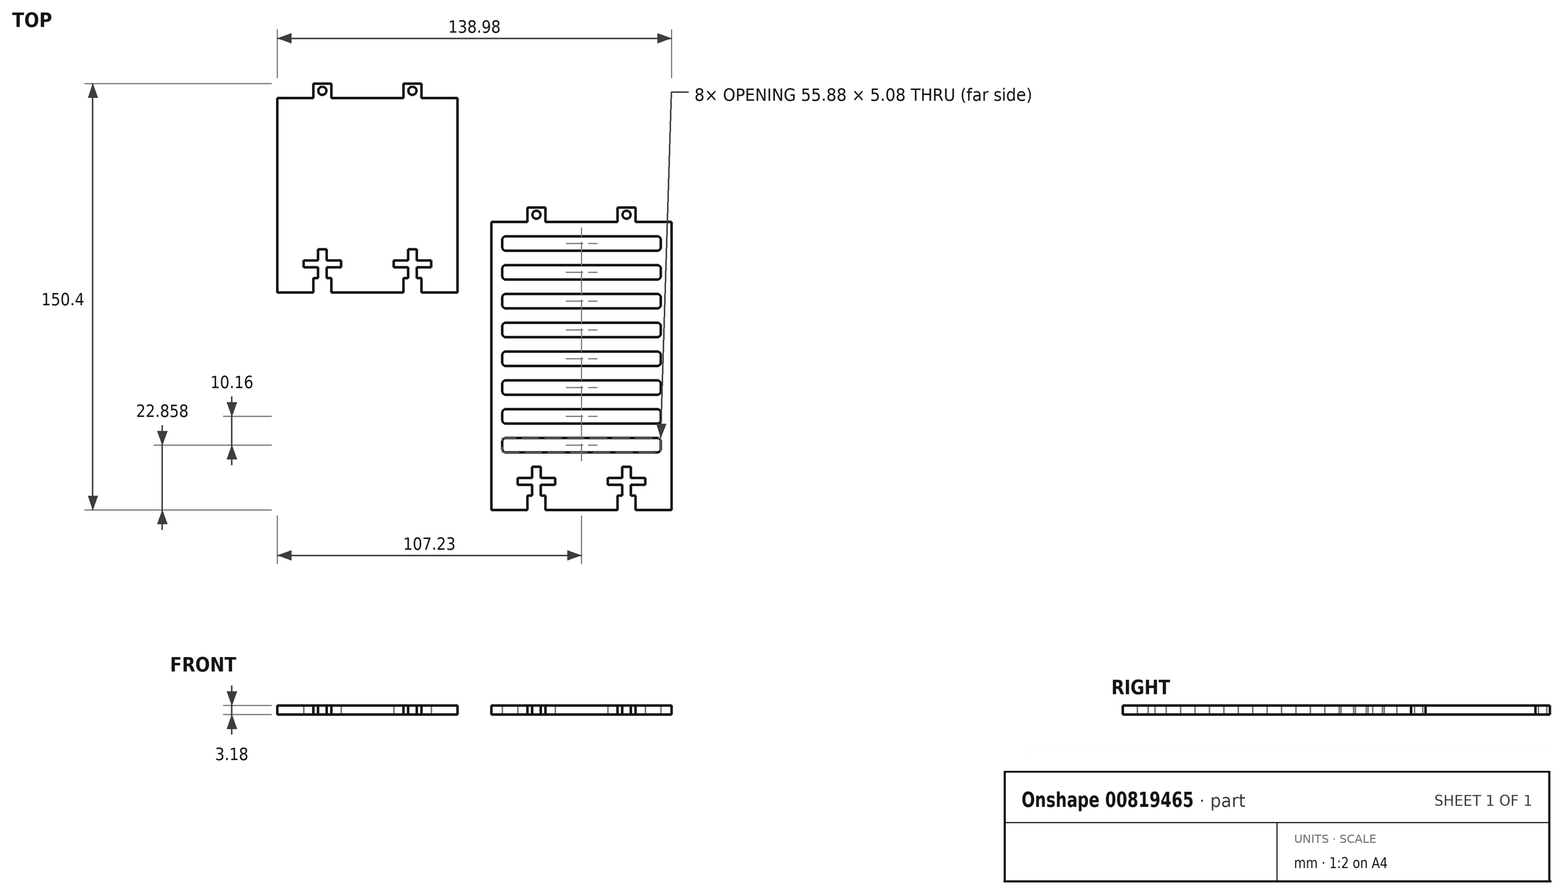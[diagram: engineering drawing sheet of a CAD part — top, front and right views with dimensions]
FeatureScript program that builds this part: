
annotation { "Feature Type Name" : "Feature", "Feature Type Description" : "" }
export const myFeature = defineFeature(function(context is Context, id is Id, definition is map)
    precondition{}
    {
        {
            var Q0;
            Q0=qCreatedBy(makeId("Top.planeOp"),FACE);
            var sketch = newSketch(context, id + "F0", { "sketchPlane" : qUnion([Q0])});
            skLineSegment(sketch, "E0.bottom", {"start": v(-19.79, 5.08) * mm, "end": v(-21.44, 5.08) * mm});
            skLineSegment(sketch, "E0.top", {"start": v(-7.09, 68.58) * mm, "end": v(-19.79, 68.58) * mm});
            skLineSegment(sketch, "E0.left", {"start": v(-7.09, 5.08) * mm, "end": v(-7.09, 68.58) * mm});
            skLineSegment(sketch, "E0.right", {"start": v(-70.59, 5.08) * mm, "end": v(-70.59, 68.58) * mm});
            skPoint(sketch, "E0.middle", {"position": v(-38.84, 36.83) * mm});
            skLineSegment(sketch, "E1", {"start": v(-54.71, 15.24) * mm, "end": v(-53.19, 15.24) * mm});
            skLineSegment(sketch, "E2", {"start": v(-53.19, 15.24) * mm, "end": v(-53.19, 11.28) * mm});
            skLineSegment(sketch, "E3", {"start": v(-53.19, 11.28) * mm, "end": v(-48.1, 11.28) * mm});
            skLineSegment(sketch, "E4", {"start": v(-48.1, 11.28) * mm, "end": v(-48.1, 8.89) * mm});
            skLineSegment(sketch, "E5", {"start": v(-48.1, 8.9) * mm, "end": v(-53.19, 8.9) * mm});
            skLineSegment(sketch, "E6", {"start": v(-53.19, 8.89) * mm, "end": v(-53.19, 5.08) * mm});
            skLineSegment(sketch, "E7.MirrorCS", {"start": v(-56.24, 15.24) * mm, "end": v(-56.24, 11.28) * mm});
            skLineSegment(sketch, "E8.MirrorCS", {"start": v(-54.71, 15.24) * mm, "end": v(-56.24, 15.24) * mm});
            skLineSegment(sketch, "E9.MirrorCS", {"start": v(-56.24, 11.28) * mm, "end": v(-61.32, 11.28) * mm});
            skLineSegment(sketch, "E10.MirrorCS", {"start": v(-61.32, 11.28) * mm, "end": v(-61.32, 8.9) * mm});
            skLineSegment(sketch, "E11.MirrorCS", {"start": v(-61.32, 8.9) * mm, "end": v(-56.24, 8.9) * mm});
            skLineSegment(sketch, "E12.MirrorCS", {"start": v(-56.24, 8.89) * mm, "end": v(-56.24, 5.08) * mm});
            skLineSegment(sketch, "E13.trimOffspring", {"start": v(-56.24, 5.08) * mm, "end": v(-57.89, 5.08) * mm});
            skLineSegment(sketch, "E14", {"start": v(-38.84, 36.83) * mm, "end": v(-38.84, 5.08) * mm, "construction": true});
            skLineSegment(sketch, "E15.MirrorCS", {"start": v(-24.49, 8.89) * mm, "end": v(-24.49, 5.08) * mm});
            skLineSegment(sketch, "E16.MirrorCS", {"start": v(-29.57, 8.9) * mm, "end": v(-24.49, 8.9) * mm});
            skLineSegment(sketch, "E17.MirrorCS", {"start": v(-29.57, 11.28) * mm, "end": v(-29.57, 8.89) * mm});
            skLineSegment(sketch, "E18.MirrorCS", {"start": v(-24.49, 11.28) * mm, "end": v(-29.57, 11.28) * mm});
            skLineSegment(sketch, "E19.MirrorCS", {"start": v(-24.49, 15.24) * mm, "end": v(-24.49, 11.28) * mm});
            skLineSegment(sketch, "E20.MirrorCS", {"start": v(-22.96, 15.24) * mm, "end": v(-24.49, 15.24) * mm});
            skLineSegment(sketch, "E21.MirrorCS", {"start": v(-22.96, 15.24) * mm, "end": v(-21.44, 15.24) * mm});
            skLineSegment(sketch, "E22.MirrorCS", {"start": v(-21.44, 15.24) * mm, "end": v(-21.44, 11.28) * mm});
            skLineSegment(sketch, "E23.MirrorCS", {"start": v(-21.44, 11.28) * mm, "end": v(-16.36, 11.28) * mm});
            skLineSegment(sketch, "E24.MirrorCS", {"start": v(-16.36, 11.28) * mm, "end": v(-16.36, 8.9) * mm});
            skLineSegment(sketch, "E25.MirrorCS", {"start": v(-16.36, 8.9) * mm, "end": v(-21.44, 8.9) * mm});
            skLineSegment(sketch, "E26.MirrorCS", {"start": v(-21.44, 8.9) * mm, "end": v(-21.44, 5.08) * mm});
            skLineSegment(sketch, "E27.trimOffspring", {"start": v(-24.49, 5.08) * mm, "end": v(-26.14, 5.08) * mm});
            skPoint(sketch, "E28", {"position": v(-54.71, 68.58) * mm});
            skPoint(sketch, "E29", {"position": v(-51.54, 68.58) * mm});
            skLineSegment(sketch, "E30", {"start": v(-54.71, 68.58) * mm, "end": v(-54.71, 51.26) * mm, "construction": true});
            skPoint(sketch, "E31.MirrorP", {"position": v(-57.89, 68.58) * mm});
            skLineSegment(sketch, "E32.trimOffspring", {"start": v(-57.89, 68.58) * mm, "end": v(-70.59, 68.58) * mm});
            skLineSegment(sketch, "E33", {"start": v(-57.89, 68.58) * mm, "end": v(-57.89, 73.66) * mm});
            skLineSegment(sketch, "E34", {"start": v(-57.89, 73.66) * mm, "end": v(-51.54, 73.66) * mm});
            skLineSegment(sketch, "E35", {"start": v(-51.54, 73.66) * mm, "end": v(-51.54, 68.58) * mm});
            skPoint(sketch, "E36", {"position": v(-54.71, 71.12) * mm});
            skCircle(sketch, "E37", {"center": v(-54.71, 71.12) * mm, "radius": 1.44 * mm});
            skLineSegment(sketch, "E38.trimOffspring", {"start": v(-53.28, 71.12) * mm, "end": v(-51.54, 71.12) * mm});
            skPoint(sketch, "E39.start.orphan", {"position": v(-57.89, 71.12) * mm});
            skLineSegment(sketch, "E40.MirrorCS", {"start": v(-19.79, 68.58) * mm, "end": v(-19.79, 73.66) * mm});
            skLineSegment(sketch, "E41.MirrorCS", {"start": v(-19.79, 73.66) * mm, "end": v(-26.14, 73.66) * mm});
            skLineSegment(sketch, "E42.MirrorCS", {"start": v(-26.14, 73.66) * mm, "end": v(-26.14, 68.58) * mm});
            skCircle(sketch, "E43.MirrorC", {"center": v(-22.96, 71.12) * mm, "radius": 1.44 * mm});
            skLineSegment(sketch, "E44.trimOffspring", {"start": v(-26.14, 68.58) * mm, "end": v(-51.54, 68.58) * mm});
            skPoint(sketch, "E45", {"position": v(-57.89, 5.08) * mm});
            skPoint(sketch, "E46", {"position": v(-51.54, 5.08) * mm});
            skPoint(sketch, "E47.MirrorP", {"position": v(-19.79, 5.08) * mm});
            skPoint(sketch, "E48.MirrorP", {"position": v(-26.14, 5.08) * mm});
            skLineSegment(sketch, "E49", {"start": v(-70.59, 5.08) * mm, "end": v(-70.59, 0) * mm});
            skLineSegment(sketch, "E50", {"start": v(-70.59, 0) * mm, "end": v(-57.89, 0) * mm});
            skLineSegment(sketch, "E51", {"start": v(-57.89, 0) * mm, "end": v(-57.89, 5.08) * mm});
            skLineSegment(sketch, "E52.MirrorCS", {"start": v(-7.09, 5.08) * mm, "end": v(-7.09, 0) * mm});
            skLineSegment(sketch, "E53.MirrorCS", {"start": v(-7.09, 0) * mm, "end": v(-19.79, 0) * mm});
            skLineSegment(sketch, "E54.MirrorCS", {"start": v(-19.79, 0) * mm, "end": v(-19.79, 5.08) * mm});
            skLineSegment(sketch, "E55", {"start": v(-51.54, 5.08) * mm, "end": v(-51.54, 0) * mm});
            skLineSegment(sketch, "E56", {"start": v(-51.54, 0) * mm, "end": v(-26.14, 0) * mm});
            skLineSegment(sketch, "E57", {"start": v(-26.14, 0) * mm, "end": v(-26.14, 5.08) * mm});
            skLineSegment(sketch, "E58.trimOffspring", {"start": v(-51.54, 5.08) * mm, "end": v(-53.19, 5.08) * mm});
            skSolve(sketch);
        }
        {
            var Q0;
            Q0=makeQuery(id+"F0.imprint","IMPRINT",FACE,{"disambiguationData":[TD([[makeQuery(id+"F0.imprint","IMPRINT",EDGE,{"derivedFrom":sQuery(id+"F0.wireOp",EDGE,"E0.bottom")}),-1.0]])]});
            extrude(context, id + "F1", {"entities" : qUnion([Q0]), "depth" : 3.17 * mm, "offsetDistance" : 25.4 * mm});
        }
        {
            var Q0;
            Q0=qCreatedBy(makeId("Top.planeOp"),FACE);
            var sketch = newSketch(context, id + "F2", { "sketchPlane" : qUnion([Q0])});
            skLineSegment(sketch, "E59.bottom", {"start": v(55.69, -71.66) * mm, "end": v(54.04, -71.66) * mm});
            skLineSegment(sketch, "E59.top", {"start": v(68.39, 24.86) * mm, "end": v(55.69, 24.86) * mm});
            skLineSegment(sketch, "E59.left", {"start": v(68.39, -71.66) * mm, "end": v(68.39, 24.86) * mm});
            skLineSegment(sketch, "E59.right", {"start": v(4.89, -71.66) * mm, "end": v(4.89, 24.86) * mm});
            skPoint(sketch, "E59.middle", {"position": v(36.64, -23.4) * mm});
            skLineSegment(sketch, "E60", {"start": v(20.76, -61.5) * mm, "end": v(22.29, -61.5) * mm});
            skLineSegment(sketch, "E61", {"start": v(22.29, -61.5) * mm, "end": v(22.29, -65.46) * mm});
            skLineSegment(sketch, "E62", {"start": v(22.29, -65.46) * mm, "end": v(27.37, -65.46) * mm});
            skLineSegment(sketch, "E63", {"start": v(27.37, -65.46) * mm, "end": v(27.37, -67.85) * mm});
            skLineSegment(sketch, "E64", {"start": v(27.37, -67.85) * mm, "end": v(22.29, -67.85) * mm});
            skLineSegment(sketch, "E65", {"start": v(22.29, -67.85) * mm, "end": v(22.29, -71.66) * mm});
            skLineSegment(sketch, "E66.MirrorCS", {"start": v(19.24, -61.5) * mm, "end": v(19.24, -65.46) * mm});
            skLineSegment(sketch, "E67.MirrorCS", {"start": v(20.76, -61.5) * mm, "end": v(19.24, -61.5) * mm});
            skLineSegment(sketch, "E68.MirrorCS", {"start": v(19.24, -65.46) * mm, "end": v(14.16, -65.46) * mm});
            skLineSegment(sketch, "E69.MirrorCS", {"start": v(14.16, -65.46) * mm, "end": v(14.16, -67.85) * mm});
            skLineSegment(sketch, "E70.MirrorCS", {"start": v(14.16, -67.85) * mm, "end": v(19.24, -67.85) * mm});
            skLineSegment(sketch, "E71.MirrorCS", {"start": v(19.24, -67.85) * mm, "end": v(19.24, -71.66) * mm});
            skLineSegment(sketch, "E72.trimOffspring", {"start": v(19.24, -71.66) * mm, "end": v(17.59, -71.66) * mm});
            skLineSegment(sketch, "E73", {"start": v(36.64, -23.4) * mm, "end": v(36.64, -71.66) * mm, "construction": true});
            skLineSegment(sketch, "E74.MirrorCS", {"start": v(51, -67.85) * mm, "end": v(51, -71.66) * mm});
            skLineSegment(sketch, "E75.MirrorCS", {"start": v(45.91, -67.85) * mm, "end": v(51, -67.85) * mm});
            skLineSegment(sketch, "E76.MirrorCS", {"start": v(45.91, -65.46) * mm, "end": v(45.91, -67.85) * mm});
            skLineSegment(sketch, "E77.MirrorCS", {"start": v(51, -65.46) * mm, "end": v(45.91, -65.46) * mm});
            skLineSegment(sketch, "E78.MirrorCS", {"start": v(51, -61.5) * mm, "end": v(51, -65.46) * mm});
            skLineSegment(sketch, "E79.MirrorCS", {"start": v(52.51, -61.5) * mm, "end": v(51, -61.5) * mm});
            skLineSegment(sketch, "E80.MirrorCS", {"start": v(52.51, -61.5) * mm, "end": v(54.04, -61.5) * mm});
            skLineSegment(sketch, "E81.MirrorCS", {"start": v(54.04, -61.5) * mm, "end": v(54.04, -65.46) * mm});
            skLineSegment(sketch, "E82.MirrorCS", {"start": v(54.04, -65.46) * mm, "end": v(59.12, -65.46) * mm});
            skLineSegment(sketch, "E83.MirrorCS", {"start": v(59.12, -65.46) * mm, "end": v(59.12, -67.85) * mm});
            skLineSegment(sketch, "E84.MirrorCS", {"start": v(59.12, -67.85) * mm, "end": v(54.04, -67.85) * mm});
            skLineSegment(sketch, "E85.MirrorCS", {"start": v(54.04, -67.85) * mm, "end": v(54.04, -71.66) * mm});
            skLineSegment(sketch, "E86.trimOffspring", {"start": v(51, -71.66) * mm, "end": v(49.34, -71.66) * mm});
            skPoint(sketch, "E87", {"position": v(20.76, 24.86) * mm});
            skPoint(sketch, "E88", {"position": v(23.94, 24.86) * mm});
            skLineSegment(sketch, "E89", {"start": v(20.76, 24.86) * mm, "end": v(20.76, 7.54) * mm, "construction": true});
            skPoint(sketch, "E90.MirrorP", {"position": v(17.59, 24.86) * mm});
            skLineSegment(sketch, "E91.trimOffspring", {"start": v(17.59, 24.86) * mm, "end": v(4.89, 24.86) * mm});
            skLineSegment(sketch, "E92", {"start": v(17.59, 24.86) * mm, "end": v(17.59, 29.94) * mm});
            skLineSegment(sketch, "E93", {"start": v(17.59, 29.94) * mm, "end": v(23.94, 29.94) * mm});
            skLineSegment(sketch, "E94", {"start": v(23.94, 29.94) * mm, "end": v(23.94, 24.86) * mm});
            skPoint(sketch, "E95", {"position": v(20.76, 27.4) * mm});
            skCircle(sketch, "E96", {"center": v(20.76, 27.4) * mm, "radius": 1.44 * mm});
            skLineSegment(sketch, "E97.trimOffspring", {"start": v(22.2, 27.4) * mm, "end": v(23.94, 27.4) * mm});
            skPoint(sketch, "E98.start.orphan", {"position": v(17.59, 27.4) * mm});
            skLineSegment(sketch, "E99.MirrorCS", {"start": v(55.69, 24.86) * mm, "end": v(55.69, 29.94) * mm});
            skLineSegment(sketch, "E100.MirrorCS", {"start": v(55.69, 29.94) * mm, "end": v(49.34, 29.94) * mm});
            skLineSegment(sketch, "E101.MirrorCS", {"start": v(49.34, 29.94) * mm, "end": v(49.34, 24.86) * mm});
            skCircle(sketch, "E102.MirrorC", {"center": v(52.51, 27.4) * mm, "radius": 1.44 * mm});
            skLineSegment(sketch, "E103.trimOffspring", {"start": v(49.34, 24.86) * mm, "end": v(23.94, 24.86) * mm});
            skPoint(sketch, "E104", {"position": v(17.59, -71.66) * mm});
            skPoint(sketch, "E105", {"position": v(23.94, -71.66) * mm});
            skPoint(sketch, "E106.MirrorP", {"position": v(55.69, -71.66) * mm});
            skPoint(sketch, "E107.MirrorP", {"position": v(49.34, -71.66) * mm});
            skLineSegment(sketch, "E108", {"start": v(4.89, -71.66) * mm, "end": v(4.89, -76.74) * mm});
            skLineSegment(sketch, "E109", {"start": v(4.89, -76.74) * mm, "end": v(17.59, -76.74) * mm});
            skLineSegment(sketch, "E110", {"start": v(17.59, -76.74) * mm, "end": v(17.59, -71.66) * mm});
            skLineSegment(sketch, "E111.MirrorCS", {"start": v(68.39, -71.66) * mm, "end": v(68.39, -76.74) * mm});
            skLineSegment(sketch, "E112.MirrorCS", {"start": v(68.39, -76.74) * mm, "end": v(55.69, -76.74) * mm});
            skLineSegment(sketch, "E113.MirrorCS", {"start": v(55.69, -76.74) * mm, "end": v(55.69, -71.66) * mm});
            skLineSegment(sketch, "E114", {"start": v(23.94, -76.74) * mm, "end": v(49.34, -76.74) * mm});
            skLineSegment(sketch, "E115.trimOffspring", {"start": v(23.94, -71.66) * mm, "end": v(22.29, -71.66) * mm});
            skLineSegment(sketch, "E116", {"start": v(23.94, -71.66) * mm, "end": v(23.94, -76.74) * mm});
            skLineSegment(sketch, "E117", {"start": v(49.34, -71.66) * mm, "end": v(49.34, -76.74) * mm});
            skPoint(sketch, "E118.middle", {"position": v(36.35, -22.54) * mm});
            skLineSegment(sketch, "E119.bottom", {"start": v(9.97, 19.78) * mm, "end": v(63.3, 19.78) * mm});
            skLineSegment(sketch, "E119.top", {"start": v(9.97, 14.7) * mm, "end": v(63.3, 14.7) * mm});
            skLineSegment(sketch, "E119.left", {"start": v(8.7, 18.5) * mm, "end": v(8.7, 15.97) * mm});
            skLineSegment(sketch, "E119.right", {"start": v(64.58, 18.5) * mm, "end": v(64.58, 15.97) * mm});
            skPoint(sketch, "E120.visualSharp", {"position": v(64.58, 14.7) * mm});
            skArc(sketch, "E120.filletArc", {"start": v(63.3, 14.7) * mm, "mid": v(64.2, 15.07) * mm, "end": v(64.58, 15.97) * mm});
            skPoint(sketch, "E121.visualSharp", {"position": v(64.58, 19.78) * mm});
            skArc(sketch, "E121.filletArc", {"start": v(64.58, 18.5) * mm, "mid": v(64.2, 19.4) * mm, "end": v(63.3, 19.78) * mm});
            skPoint(sketch, "E122.visualSharp", {"position": v(8.7, 14.7) * mm});
            skArc(sketch, "E122.filletArc", {"start": v(8.7, 15.97) * mm, "mid": v(9.07, 15.07) * mm, "end": v(9.97, 14.7) * mm});
            skPoint(sketch, "E123.visualSharp", {"position": v(8.7, 19.78) * mm});
            skArc(sketch, "E123.filletArc", {"start": v(9.97, 19.78) * mm, "mid": v(9.07, 19.4) * mm, "end": v(8.7, 18.5) * mm});
            skLineSegment(sketch, "E124.bottom", {"start": v(9.97, 9.62) * mm, "end": v(63.3, 9.62) * mm});
            skLineSegment(sketch, "E124.top", {"start": v(9.97, 4.54) * mm, "end": v(63.3, 4.54) * mm});
            skLineSegment(sketch, "E124.left", {"start": v(8.7, 8.35) * mm, "end": v(8.7, 5.8) * mm});
            skLineSegment(sketch, "E124.right", {"start": v(64.58, 8.35) * mm, "end": v(64.58, 5.8) * mm});
            skPoint(sketch, "E125.visualSharp", {"position": v(64.58, 4.54) * mm});
            skArc(sketch, "E125.filletArc", {"start": v(63.3, 4.54) * mm, "mid": v(64.2, 4.91) * mm, "end": v(64.58, 5.8) * mm});
            skPoint(sketch, "E126.visualSharp", {"position": v(64.58, 9.62) * mm});
            skArc(sketch, "E126.filletArc", {"start": v(64.58, 8.35) * mm, "mid": v(64.2, 9.25) * mm, "end": v(63.3, 9.62) * mm});
            skPoint(sketch, "E127.visualSharp", {"position": v(8.7, 4.54) * mm});
            skArc(sketch, "E127.filletArc", {"start": v(8.7, 5.8) * mm, "mid": v(9.07, 4.91) * mm, "end": v(9.97, 4.54) * mm});
            skPoint(sketch, "E128.visualSharp", {"position": v(8.7, 9.62) * mm});
            skArc(sketch, "E128.filletArc", {"start": v(9.97, 9.62) * mm, "mid": v(9.07, 9.25) * mm, "end": v(8.7, 8.35) * mm});
            skLineSegment(sketch, "E129.bottom", {"start": v(9.97, -0.54) * mm, "end": v(63.3, -0.54) * mm});
            skLineSegment(sketch, "E129.top", {"start": v(9.97, -5.62) * mm, "end": v(63.3, -5.62) * mm});
            skLineSegment(sketch, "E129.left", {"start": v(8.7, -1.81) * mm, "end": v(8.7, -4.35) * mm});
            skLineSegment(sketch, "E129.right", {"start": v(64.58, -1.81) * mm, "end": v(64.58, -4.35) * mm});
            skPoint(sketch, "E130.visualSharp", {"position": v(64.58, -5.62) * mm});
            skArc(sketch, "E130.filletArc", {"start": v(63.3, -5.62) * mm, "mid": v(64.2, -5.25) * mm, "end": v(64.58, -4.35) * mm});
            skPoint(sketch, "E131.visualSharp", {"position": v(64.58, -0.54) * mm});
            skArc(sketch, "E131.filletArc", {"start": v(64.58, -1.81) * mm, "mid": v(64.2, -0.91) * mm, "end": v(63.3, -0.54) * mm});
            skPoint(sketch, "E132.visualSharp", {"position": v(8.7, -5.62) * mm});
            skArc(sketch, "E132.filletArc", {"start": v(8.7, -4.35) * mm, "mid": v(9.07, -5.25) * mm, "end": v(9.97, -5.62) * mm});
            skPoint(sketch, "E133.visualSharp", {"position": v(8.7, -0.54) * mm});
            skArc(sketch, "E133.filletArc", {"start": v(9.97, -0.54) * mm, "mid": v(9.07, -0.91) * mm, "end": v(8.7, -1.81) * mm});
            skLineSegment(sketch, "E134.bottom", {"start": v(9.97, -10.7) * mm, "end": v(63.3, -10.7) * mm});
            skLineSegment(sketch, "E134.top", {"start": v(9.97, -15.78) * mm, "end": v(63.3, -15.78) * mm});
            skLineSegment(sketch, "E134.left", {"start": v(8.7, -11.97) * mm, "end": v(8.7, -14.51) * mm});
            skLineSegment(sketch, "E134.right", {"start": v(64.58, -11.97) * mm, "end": v(64.58, -14.51) * mm});
            skPoint(sketch, "E135.visualSharp", {"position": v(64.58, -15.78) * mm});
            skArc(sketch, "E135.filletArc", {"start": v(63.3, -15.78) * mm, "mid": v(64.2, -15.4) * mm, "end": v(64.58, -14.51) * mm});
            skPoint(sketch, "E136.visualSharp", {"position": v(64.58, -10.7) * mm});
            skArc(sketch, "E136.filletArc", {"start": v(64.58, -11.97) * mm, "mid": v(64.2, -11.07) * mm, "end": v(63.3, -10.7) * mm});
            skPoint(sketch, "E137.visualSharp", {"position": v(8.7, -15.78) * mm});
            skArc(sketch, "E137.filletArc", {"start": v(8.7, -14.51) * mm, "mid": v(9.07, -15.4) * mm, "end": v(9.97, -15.78) * mm});
            skPoint(sketch, "E138.visualSharp", {"position": v(8.7, -10.7) * mm});
            skArc(sketch, "E138.filletArc", {"start": v(9.97, -10.7) * mm, "mid": v(9.07, -11.07) * mm, "end": v(8.7, -11.97) * mm});
            skLineSegment(sketch, "E139.bottom", {"start": v(9.97, -20.86) * mm, "end": v(63.3, -20.86) * mm});
            skLineSegment(sketch, "E139.top", {"start": v(9.97, -25.94) * mm, "end": v(63.3, -25.94) * mm});
            skLineSegment(sketch, "E139.left", {"start": v(8.7, -22.13) * mm, "end": v(8.7, -24.67) * mm});
            skLineSegment(sketch, "E139.right", {"start": v(64.58, -22.13) * mm, "end": v(64.58, -24.67) * mm});
            skPoint(sketch, "E140.visualSharp", {"position": v(64.58, -25.94) * mm});
            skArc(sketch, "E140.filletArc", {"start": v(63.3, -25.94) * mm, "mid": v(64.2, -25.57) * mm, "end": v(64.58, -24.67) * mm});
            skPoint(sketch, "E141.visualSharp", {"position": v(64.58, -20.86) * mm});
            skArc(sketch, "E141.filletArc", {"start": v(64.58, -22.13) * mm, "mid": v(64.2, -21.23) * mm, "end": v(63.3, -20.86) * mm});
            skPoint(sketch, "E142.visualSharp", {"position": v(8.7, -25.94) * mm});
            skArc(sketch, "E142.filletArc", {"start": v(8.7, -24.67) * mm, "mid": v(9.07, -25.57) * mm, "end": v(9.97, -25.94) * mm});
            skPoint(sketch, "E143.visualSharp", {"position": v(8.7, -20.86) * mm});
            skArc(sketch, "E143.filletArc", {"start": v(9.97, -20.86) * mm, "mid": v(9.07, -21.23) * mm, "end": v(8.7, -22.13) * mm});
            skLineSegment(sketch, "E144.bottom", {"start": v(9.97, -31.02) * mm, "end": v(63.3, -31.02) * mm});
            skLineSegment(sketch, "E144.top", {"start": v(9.97, -36.1) * mm, "end": v(63.3, -36.1) * mm});
            skLineSegment(sketch, "E144.left", {"start": v(8.7, -32.3) * mm, "end": v(8.7, -34.83) * mm});
            skLineSegment(sketch, "E144.right", {"start": v(64.58, -32.3) * mm, "end": v(64.58, -34.83) * mm});
            skPoint(sketch, "E145.visualSharp", {"position": v(64.58, -36.1) * mm});
            skArc(sketch, "E145.filletArc", {"start": v(63.3, -36.1) * mm, "mid": v(64.2, -35.73) * mm, "end": v(64.58, -34.83) * mm});
            skPoint(sketch, "E146.visualSharp", {"position": v(64.58, -31.02) * mm});
            skArc(sketch, "E146.filletArc", {"start": v(64.58, -32.3) * mm, "mid": v(64.2, -31.4) * mm, "end": v(63.3, -31.02) * mm});
            skPoint(sketch, "E147.visualSharp", {"position": v(8.7, -36.1) * mm});
            skArc(sketch, "E147.filletArc", {"start": v(8.7, -34.83) * mm, "mid": v(9.07, -35.73) * mm, "end": v(9.97, -36.1) * mm});
            skPoint(sketch, "E148.visualSharp", {"position": v(8.7, -31.02) * mm});
            skArc(sketch, "E148.filletArc", {"start": v(9.97, -31.02) * mm, "mid": v(9.07, -31.4) * mm, "end": v(8.7, -32.3) * mm});
            skLineSegment(sketch, "E149.bottom", {"start": v(9.97, -41.18) * mm, "end": v(63.3, -41.18) * mm});
            skLineSegment(sketch, "E149.top", {"start": v(9.97, -46.26) * mm, "end": v(63.3, -46.26) * mm});
            skLineSegment(sketch, "E149.left", {"start": v(8.7, -42.45) * mm, "end": v(8.7, -45) * mm});
            skLineSegment(sketch, "E149.right", {"start": v(64.58, -42.45) * mm, "end": v(64.58, -45) * mm});
            skPoint(sketch, "E150.visualSharp", {"position": v(64.58, -46.26) * mm});
            skArc(sketch, "E150.filletArc", {"start": v(63.3, -46.26) * mm, "mid": v(64.2, -45.89) * mm, "end": v(64.58, -45) * mm});
            skPoint(sketch, "E151.visualSharp", {"position": v(64.58, -41.18) * mm});
            skArc(sketch, "E151.filletArc", {"start": v(64.58, -42.45) * mm, "mid": v(64.2, -41.55) * mm, "end": v(63.3, -41.18) * mm});
            skPoint(sketch, "E152.visualSharp", {"position": v(8.7, -46.26) * mm});
            skArc(sketch, "E152.filletArc", {"start": v(8.7, -45) * mm, "mid": v(9.07, -45.89) * mm, "end": v(9.97, -46.26) * mm});
            skPoint(sketch, "E153.visualSharp", {"position": v(8.7, -41.18) * mm});
            skArc(sketch, "E153.filletArc", {"start": v(9.97, -41.18) * mm, "mid": v(9.07, -41.55) * mm, "end": v(8.7, -42.45) * mm});
            skLineSegment(sketch, "E154.bottom", {"start": v(9.97, -51.34) * mm, "end": v(63.3, -51.34) * mm});
            skLineSegment(sketch, "E154.top", {"start": v(9.97, -56.42) * mm, "end": v(63.3, -56.42) * mm});
            skLineSegment(sketch, "E154.left", {"start": v(8.7, -52.61) * mm, "end": v(8.7, -55.15) * mm});
            skLineSegment(sketch, "E154.right", {"start": v(64.58, -52.61) * mm, "end": v(64.58, -55.15) * mm});
            skPoint(sketch, "E155.visualSharp", {"position": v(64.58, -56.42) * mm});
            skArc(sketch, "E155.filletArc", {"start": v(63.3, -56.42) * mm, "mid": v(64.2, -56.05) * mm, "end": v(64.58, -55.15) * mm});
            skPoint(sketch, "E156.visualSharp", {"position": v(64.58, -51.34) * mm});
            skArc(sketch, "E156.filletArc", {"start": v(64.58, -52.61) * mm, "mid": v(64.2, -51.71) * mm, "end": v(63.3, -51.34) * mm});
            skPoint(sketch, "E157.visualSharp", {"position": v(8.7, -56.42) * mm});
            skArc(sketch, "E157.filletArc", {"start": v(8.7, -55.15) * mm, "mid": v(9.07, -56.05) * mm, "end": v(9.97, -56.42) * mm});
            skPoint(sketch, "E158.visualSharp", {"position": v(8.7, -51.34) * mm});
            skArc(sketch, "E158.filletArc", {"start": v(9.97, -51.34) * mm, "mid": v(9.07, -51.71) * mm, "end": v(8.7, -52.61) * mm});
            skSolve(sketch);
        }
        {
            var Q0;
            Q0=makeQuery(id+"F2.imprint","IMPRINT",FACE,{"disambiguationData":[TD([[makeQuery(id+"F2.imprint","IMPRINT",EDGE,{"derivedFrom":sQuery(id+"F2.wireOp",EDGE,"E59.bottom")}),-1.0]])]});
            extrude(context, id + "F3", {"entities" : qUnion([Q0]), "depth" : 3.17 * mm, "offsetDistance" : 25.4 * mm});
        }
    });
